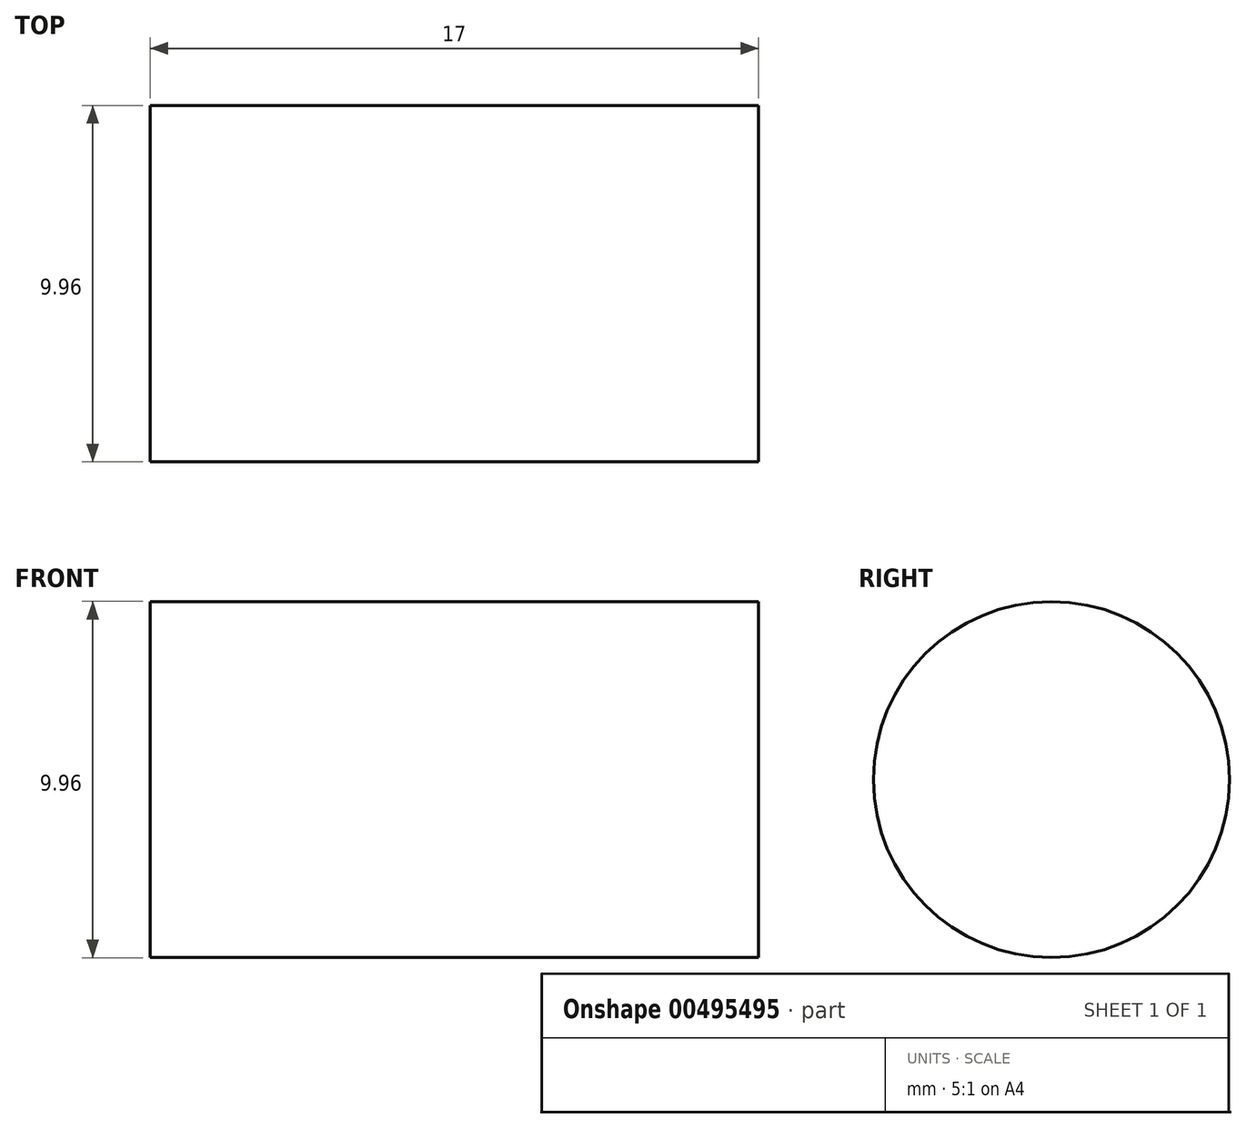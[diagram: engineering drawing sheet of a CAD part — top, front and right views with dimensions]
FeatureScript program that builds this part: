
annotation { "Feature Type Name" : "Feature", "Feature Type Description" : "" }
export const myFeature = defineFeature(function(context is Context, id is Id, definition is map)
    precondition{}
    {
        {
            var Q0;
            Q0=qCreatedBy(makeId("Front.planeOp"),FACE);
            var sketch = newSketch(context, id + "F0", { "sketchPlane" : qUnion([Q0])});
            skLineSegment(sketch, "E0", {"start": v(0, 0) * mm, "end": v(0, 19.75) * mm, "construction": true});
            skLineSegment(sketch, "E1", {"start": v(0, 0) * mm, "end": v(-28.63, 0) * mm, "construction": true});
            skLineSegment(sketch, "E2.bottom", {"start": v(0, 0) * mm, "end": v(-17, 0) * mm});
            skLineSegment(sketch, "E2.top", {"start": v(0, 4.97) * mm, "end": v(-17, 4.97) * mm});
            skLineSegment(sketch, "E2.left", {"start": v(0, 0) * mm, "end": v(0, 4.97) * mm});
            skLineSegment(sketch, "E2.right", {"start": v(-17, 0) * mm, "end": v(-17, 4.97) * mm});
            skSolve(sketch);
        }
        {
            var Q0;
            Q0 = qSketchRegion(id + "F0", true);
            var Q1;
            Q1=sQuery(id+"F0.wireOp",EDGE,"E1");
            revolve(context, id + "F1", {"entities" : qUnion([Q0]), "axis" : qUnion([Q1]), "revolveType" : RevolveType.FULL});
        }
    });
